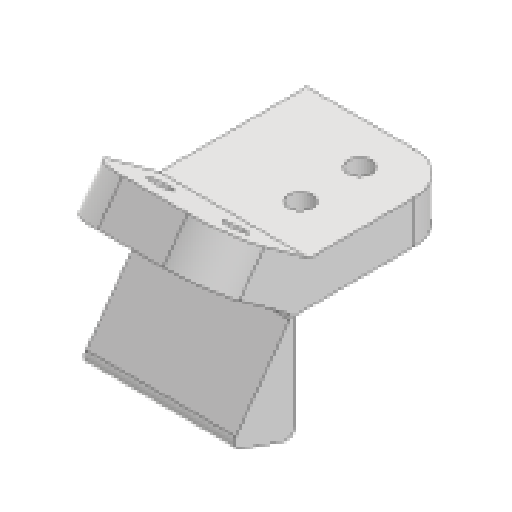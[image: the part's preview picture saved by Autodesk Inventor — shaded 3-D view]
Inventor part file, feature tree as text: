
AUTODESK INVENTOR PART (.ipt)
format: ipt  version: 2025 (Build 290162000, 162)  size: 200,704 bytes
history: native  units: mm
features: reference x8, extrude x4, sketch x4, projected_geometry x4, other x4, fillet x3, mirror x1
ambient origin geometry x8: Origin, YZ Plane, XZ Plane, XY Plane, X Axis, Y Axis, Z Axis, Center Point
bodies: Solid1 (feature_tree)
feature tree (28):
  extrude  "Extrusion1"  Depth=38.1mm
  extrude  "Extrusion2"  Depth=10.0mm TaperAngle=0.0deg
  extrude  "Extrusion3"  Depth=35.4mm TaperAngle=0.0deg
  extrude  "Extrusion4"  Depth=35.4mm TaperAngle=0.0deg
  fillet  "Fillet1"  Radius=2.6mm
  fillet  "Fillet2"  Radius=35.4mm
  fillet  "Fillet3"  Radius=10.0mm
  mirror  "Mirror1"
  sketch  "Sketch1"  dims[d0=25.4mm d1=38.1mm]
  sketch  "Sketch2"  dims[d2=5.5mm d3=10.0mm d4=0.0mm]
  reference  "Reference1"
  reference  "Reference2"
  reference  "Reference3"
  reference  "Reference4"
  reference  "Reference5"
  reference  "Reference6"
  reference  "Reference7"
  reference  "Reference8"
  projected_geometry  "Projected Loop1"
  sketch  "Sketch3"  dims[d5=10.0mm d8=35.4mm d9=0.0mm]
  projected_geometry  "Projected Loop2"
  projected_geometry  "Projected Loop3"
  sketch  "Sketch4"  dims[d10=10.0mm d11=35.4mm d12=0.0mm d13=2.6mm d14=35.4mm d15=0.0mm d16=10.0mm d17=2.0mm d18=1.0mm d7=0.5mm]
  projected_geometry  "Projected Loop4"
  other  "<userpath>\Desktop\puppycat\woodhouseMK1.iam"
  other  "woodhouseMK1.iam"
  other  "12inStrut:1"
  other  "trackBase:1"
